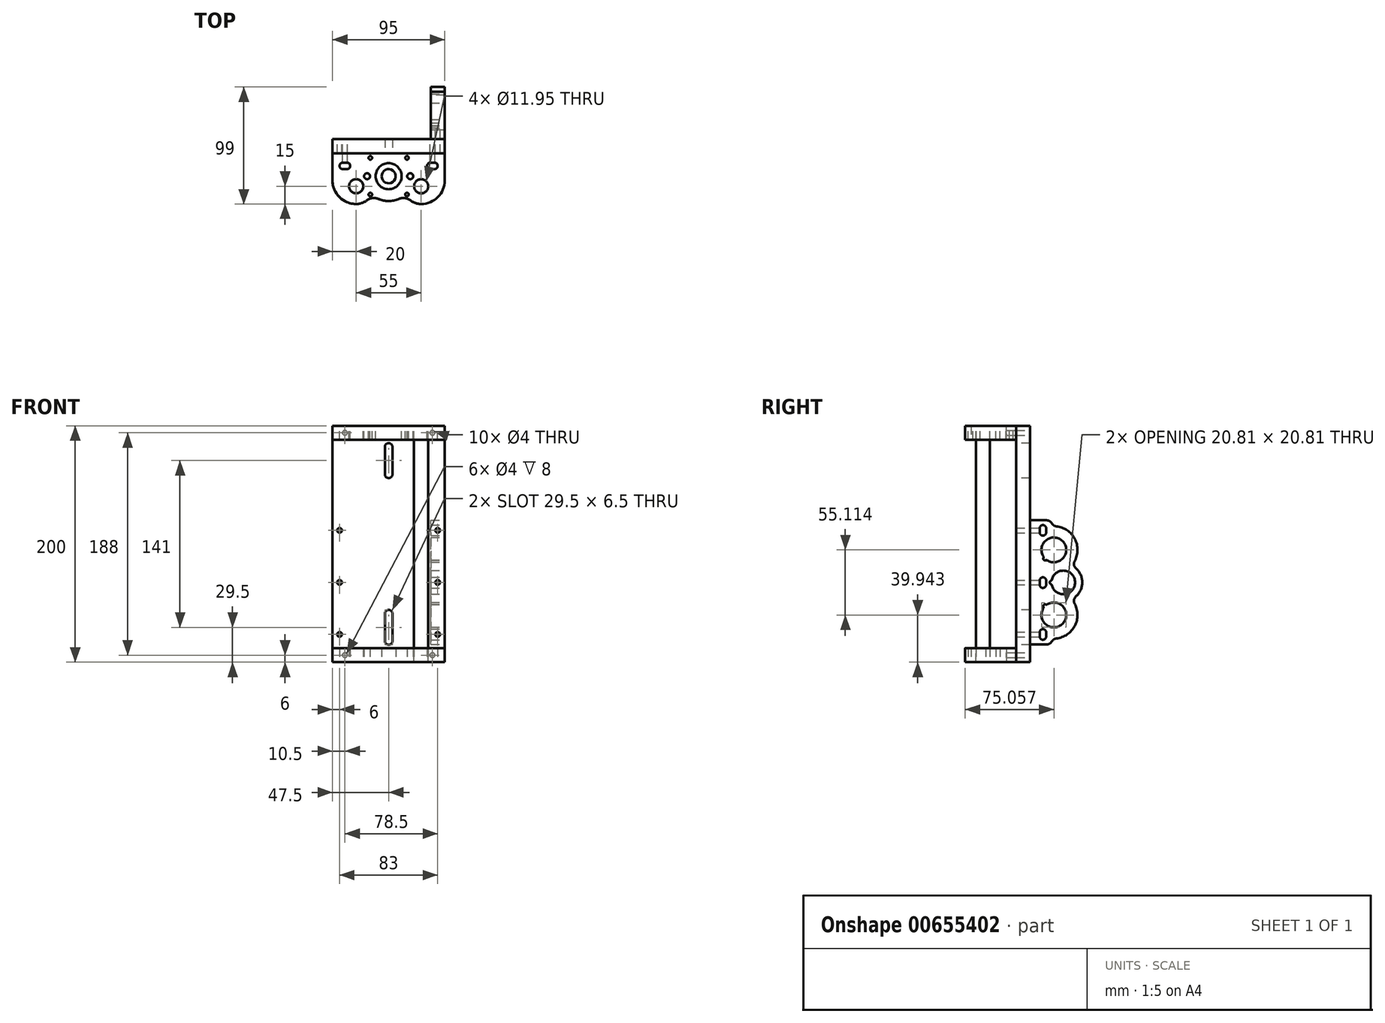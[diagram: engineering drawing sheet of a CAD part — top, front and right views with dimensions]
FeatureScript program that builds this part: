
annotation { "Feature Type Name" : "Feature", "Feature Type Description" : "" }
export const myFeature = defineFeature(function(context is Context, id is Id, definition is map)
    precondition{}
    {
        {
            var Q0;
            Q0=qCreatedBy(makeId("Front.planeOp"),FACE);
            var sketch = newSketch(context, id + "F0", { "sketchPlane" : qUnion([Q0])});
            skLineSegment(sketch, "E0.bottom", {"start": v(47.5, 0) * mm, "end": v(-47.5, 0) * mm});
            skLineSegment(sketch, "E0.top", {"start": v(-47.5, 200) * mm, "end": v(47.5, 200) * mm});
            skLineSegment(sketch, "E0.left", {"start": v(-47.5, 0) * mm, "end": v(-47.5, 200) * mm});
            skLineSegment(sketch, "E0.right", {"start": v(47.5, 0) * mm, "end": v(47.5, 200) * mm});
            skLineSegment(sketch, "E1.left", {"start": v(3.25, 182) * mm, "end": v(3.25, 159) * mm});
            skLineSegment(sketch, "E1.right", {"start": v(-3.25, 182) * mm, "end": v(-3.25, 159) * mm});
            skArc(sketch, "E2", {"start": v(3.25, 182) * mm, "mid": v(0, 185.25) * mm, "end": v(-3.25, 182) * mm});
            skArc(sketch, "E3", {"start": v(-3.25, 159) * mm, "mid": v(0, 155.75) * mm, "end": v(3.25, 159) * mm});
            skLineSegment(sketch, "E4", {"start": v(0, 200) * mm, "end": v(0, 182) * mm, "construction": true});
            skLineSegment(sketch, "E5.left", {"start": v(-3.25, 18) * mm, "end": v(-3.25, 41) * mm});
            skLineSegment(sketch, "E5.right", {"start": v(3.25, 18) * mm, "end": v(3.25, 41) * mm});
            skArc(sketch, "E6", {"start": v(-3.25, 18) * mm, "mid": v(0, 14.75) * mm, "end": v(3.25, 18) * mm});
            skArc(sketch, "E7", {"start": v(3.25, 41) * mm, "mid": v(0, 44.25) * mm, "end": v(-3.25, 41) * mm});
            skLineSegment(sketch, "E8", {"start": v(0, 0) * mm, "end": v(0, 18) * mm, "construction": true});
            skSolve(sketch);
        }
        {
            var Q0;
            Q0=qSketchRegion(id+"F0",true);
            extrude(context, id + "F1", {"entities" : qUnion([Q0]), "oppositeDirection" : true, "depth" : 12 * mm, "offsetDistance" : 25 * mm});
        }
        {
            var Q0;
            Q0=makeQuery(id+"F1.opExtrude","SWEPT_FACE",FACE,{"disambiguationData":[OSD([sQuery(id+"F0.wireOp",EDGE,"E0.top")])]});
            var sketch = newSketch(context, id + "F2", { "sketchPlane" : qUnion([Q0])});
            skLineSegment(sketch, "E9.bottom", {"start": v(-47.5, 0) * mm, "end": v(47.5, 0) * mm});
            skLineSegment(sketch, "E9.top", {"start": v(-27.5, -43) * mm, "end": v(27.5, -43) * mm, "construction": true});
            skLineSegment(sketch, "E9.left", {"start": v(-47.5, 0) * mm, "end": v(-47.5, -23) * mm});
            skLineSegment(sketch, "E9.right", {"start": v(47.5, 0) * mm, "end": v(47.5, -23) * mm});
            skLineSegment(sketch, "E10", {"start": v(0, 0) * mm, "end": v(0, -43) * mm, "construction": true});
            skCircle(sketch, "E11", {"center": v(-27.5, -28) * mm, "radius": 5.97 * mm});
            skCircle(sketch, "E12.MirrorC", {"center": v(27.5, -28) * mm, "radius": 5.97 * mm});
            skArc(sketch, "E13.filletArc", {"start": v(-47.5, -23) * mm, "mid": v(-41.64, -37.14) * mm, "end": v(-27.5, -43) * mm});
            skPoint(sketch, "E14.visualSharp", {"position": v(47.5, -43) * mm});
            skArc(sketch, "E14.filletArc", {"start": v(27.5, -43) * mm, "mid": v(41.64, -37.14) * mm, "end": v(47.5, -23) * mm});
            skCircle(sketch, "E15", {"center": v(0, -19.5) * mm, "radius": 11 * mm});
            skCircle(sketch, "E16", {"center": v(-18.25, -19.5) * mm, "radius": 2.5 * mm});
            skCircle(sketch, "E17.MirrorC", {"center": v(18.25, -19.5) * mm, "radius": 2.5 * mm});
            skLineSegment(sketch, "E18.bottom", {"start": v(-38.75, -8) * mm, "end": v(-35.25, -8) * mm});
            skLineSegment(sketch, "E18.top", {"start": v(-38.75, -13.5) * mm, "end": v(-35.25, -13.5) * mm});
            skArc(sketch, "E19", {"start": v(-38.75, -8) * mm, "mid": v(-41.5, -10.75) * mm, "end": v(-38.75, -13.5) * mm});
            skArc(sketch, "E20", {"start": v(-35.25, -13.5) * mm, "mid": v(-32.5, -10.75) * mm, "end": v(-35.25, -8) * mm});
            skLineSegment(sketch, "E21", {"start": v(-37, -8) * mm, "end": v(-37, -13.5) * mm, "construction": true});
            skArc(sketch, "E22.MirrorCS", {"start": v(35.25, -13.5) * mm, "mid": v(32.5, -10.75) * mm, "end": v(35.25, -8) * mm});
            skLineSegment(sketch, "E23.MirrorCS", {"start": v(38.75, -13.5) * mm, "end": v(35.25, -13.5) * mm});
            skLineSegment(sketch, "E24.MirrorCS", {"start": v(38.75, -8) * mm, "end": v(35.25, -8) * mm});
            skArc(sketch, "E25.MirrorCS", {"start": v(38.75, -8) * mm, "mid": v(41.5, -10.75) * mm, "end": v(38.75, -13.5) * mm});
            skArc(sketch, "E26", {"start": v(-7.8, 0) * mm, "mid": v(0, -40.5) * mm, "end": v(7.8, 0) * mm});
            skCircle(sketch, "E27", {"center": v(-27.5, -28) * mm, "radius": 15 * mm});
            skCircle(sketch, "E28", {"center": v(27.5, -28) * mm, "radius": 15 * mm});
            skSolve(sketch);
        }
        {
            var Q0;
            Q0=qSketchRegion(id+"F2",true);
            extrude(context, id + "F3", {"entities" : qUnion([Q0]), "oppositeDirection" : true, "depth" : 12 * mm, "offsetDistance" : 25 * mm});
        }
        {
            var Q0;
            Q0=makeQuery(id+"F3.opExtrude","SWEPT_EDGE",EDGE,{"disambiguationData":[OSD([sQuery(id+"F2.wireOp",EDGE,"E26"),sQuery(id+"F2.wireOp",EDGE,"E27")])]});
            var Q1;
            Q1=makeQuery(id+"F3.opExtrude","SWEPT_EDGE",EDGE,{"disambiguationData":[OSD([sQuery(id+"F2.wireOp",EDGE,"E26"),sQuery(id+"F2.wireOp",EDGE,"E28")])]});
            fillet(context, id + "F4", {"entities" : qUnion([Q0, Q1]), "radius" : 10 * mm, "tangentPropagation" : true, "allowEdgeOverflow" : false});
        }
        {
            var Q0;
            Q0=makeQuery(id+"F3.opExtrude","CAP_FACE",FACE,{"disambiguationData":[OSD([sQuery(id+"F2.wireOp",EDGE,"E9.bottom"),sQuery(id+"F2.wireOp",EDGE,"E9.top"),sQuery(id+"F2.wireOp",EDGE,"E9.left"),sQuery(id+"F2.wireOp",EDGE,"E9.right"),sQuery(id+"F2.wireOp",EDGE,"E11"),sQuery(id+"F2.wireOp",EDGE,"E12.MirrorC"),sQuery(id+"F2.wireOp",EDGE,"E13.filletArc"),sQuery(id+"F2.wireOp",EDGE,"E14.filletArc")])],"isStart":true});
            var sketch = newSketch(context, id + "F5", { "sketchPlane" : qUnion([Q0])});
            skCircle(sketch, "E29", {"center": v(27.5, -28) * mm, "radius": 6 * mm});
            skSolve(sketch);
        }
        {
            var Q0;
            Q0=qSketchRegion(id+"F5",true);
            extrude(context, id + "F6", {"entities" : qUnion([Q0]), "oppositeDirection" : true, "depth" : 200 * mm, "offsetDistance" : 25 * mm});
        }
        {
            var Q0;
            Q0=makeQuery(id+"F1.opExtrude","SWEPT_FACE",FACE,{"disambiguationData":[OSD([sQuery(id+"F0.wireOp",EDGE,"E0.right")])]});
            var sketch = newSketch(context, id + "F7", { "sketchPlane" : qUnion([Q0])});
            skLineSegment(sketch, "E30.top", {"start": v(52, 40) * mm, "end": v(52, 67.5) * mm, "construction": true});
            skLineSegment(sketch, "E31", {"start": v(12, 67.5) * mm, "end": v(52, 67.5) * mm, "construction": true});
            skPoint(sketch, "E32.centerSnap0", {"position": v(32, 67.5) * mm});
            skArc(sketch, "E33.filletArc", {"start": v(32, 20) * mm, "mid": v(46.14, 25.86) * mm, "end": v(52, 40) * mm});
            skArc(sketch, "E34.filletArc", {"start": v(52, 95) * mm, "mid": v(46.14, 109.14) * mm, "end": v(32, 115) * mm});
            skArc(sketch, "E35", {"start": v(23.22, 45.7) * mm, "mid": v(39.4, 32.6) * mm, "end": v(26.3, 48.78) * mm});
            skArc(sketch, "E36.MirrorC", {"start": v(23.22, 89.3) * mm, "mid": v(39.4, 102.4) * mm, "end": v(26.3, 86.22) * mm});
            skArc(sketch, "E37", {"start": v(47.07, 53.15) * mm, "mid": v(56, 67.5) * mm, "end": v(47.07, 81.85) * mm});
            skArc(sketch, "E38", {"start": v(30.26, 65.33) * mm, "mid": v(49.98, 67.5) * mm, "end": v(30.26, 69.67) * mm});
            skLineSegment(sketch, "E39.bottom", {"start": v(32, 20) * mm, "end": v(28.5, 15) * mm});
            skLineSegment(sketch, "E39.right", {"start": v(28.5, 15) * mm, "end": v(12, 15) * mm});
            skLineSegment(sketch, "E40.bottom", {"start": v(25.5, 25.25) * mm, "end": v(25.5, 21.75) * mm});
            skLineSegment(sketch, "E40.top", {"start": v(20, 25.25) * mm, "end": v(20, 21.75) * mm});
            skArc(sketch, "E41", {"start": v(25.5, 25.25) * mm, "mid": v(22.75, 28) * mm, "end": v(20, 25.25) * mm});
            skArc(sketch, "E42", {"start": v(20, 21.75) * mm, "mid": v(22.75, 19) * mm, "end": v(25.5, 21.75) * mm});
            skLineSegment(sketch, "E43.MirrorCS", {"start": v(32, 115) * mm, "end": v(28.5, 120) * mm});
            skLineSegment(sketch, "E44.MirrorCS", {"start": v(28.5, 120) * mm, "end": v(12, 120) * mm});
            skLineSegment(sketch, "E45.top", {"start": v(20, 69.07) * mm, "end": v(20, 65.57) * mm});
            skArc(sketch, "E46", {"start": v(25.5, 69.07) * mm, "mid": v(22.75, 71.82) * mm, "end": v(20, 69.07) * mm});
            skArc(sketch, "E47", {"start": v(20, 65.57) * mm, "mid": v(22.75, 62.82) * mm, "end": v(25.5, 65.57) * mm});
            skLineSegment(sketch, "E48", {"start": v(20, 23.5) * mm, "end": v(25.5, 23.5) * mm, "construction": true});
            skLineSegment(sketch, "E49.trimOffspring", {"start": v(52, 67.5) * mm, "end": v(52, 95) * mm, "construction": true});
            skLineSegment(sketch, "E50", {"start": v(12, 120) * mm, "end": v(12, 15) * mm});
            skLineSegment(sketch, "E51", {"start": v(32, 40) * mm, "end": v(32, 20) * mm, "construction": true});
            skLineSegment(sketch, "E52", {"start": v(32, 95) * mm, "end": v(32, 40) * mm, "construction": true});
            skArc(sketch, "E53", {"start": v(52, 40) * mm, "mid": v(50.73, 47.02) * mm, "end": v(47.07, 53.15) * mm});
            skArc(sketch, "E54.MirrorCS", {"start": v(52, 95) * mm, "mid": v(50.73, 87.98) * mm, "end": v(47.07, 81.85) * mm});
            skLineSegment(sketch, "E55", {"start": v(32, 95) * mm, "end": v(24.6, 87.6) * mm, "construction": true});
            skArc(sketch, "E56", {"start": v(23.26, 88.29) * mm, "mid": v(23.53, 86.53) * mm, "end": v(25.29, 86.26) * mm});
            skPoint(sketch, "E57.visualSharp", {"position": v(23.61, 88.73) * mm});
            skArc(sketch, "E57.filletArc", {"start": v(23.26, 88.29) * mm, "mid": v(23.38, 88.8) * mm, "end": v(23.22, 89.3) * mm});
            skPoint(sketch, "E58.visualSharp", {"position": v(25.73, 86.61) * mm});
            skArc(sketch, "E58.filletArc", {"start": v(26.3, 86.22) * mm, "mid": v(25.8, 86.38) * mm, "end": v(25.29, 86.26) * mm});
            skArc(sketch, "E59.MirrorCS", {"start": v(26.3, 48.78) * mm, "mid": v(25.8, 48.62) * mm, "end": v(25.29, 48.74) * mm});
            skArc(sketch, "E60.MirrorCS", {"start": v(23.26, 46.71) * mm, "mid": v(23.53, 48.47) * mm, "end": v(25.29, 48.74) * mm});
            skArc(sketch, "E61.MirrorCS", {"start": v(23.26, 46.71) * mm, "mid": v(23.38, 46.2) * mm, "end": v(23.22, 45.7) * mm});
            skLineSegment(sketch, "E62", {"start": v(25.5, 69.07) * mm, "end": v(25.5, 65.57) * mm});
            skArc(sketch, "E63.MirrorCS", {"start": v(25.5, 109.75) * mm, "mid": v(22.75, 107) * mm, "end": v(20, 109.75) * mm});
            skLineSegment(sketch, "E64.MirrorCS", {"start": v(25.5, 109.75) * mm, "end": v(25.5, 113.25) * mm});
            skLineSegment(sketch, "E65.MirrorCS", {"start": v(20, 109.75) * mm, "end": v(20, 113.25) * mm});
            skArc(sketch, "E66.MirrorCS", {"start": v(20, 113.25) * mm, "mid": v(22.75, 116) * mm, "end": v(25.5, 113.25) * mm});
            skArc(sketch, "E67", {"start": v(29.58, 68.93) * mm, "mid": v(28.53, 67.5) * mm, "end": v(29.58, 66.07) * mm});
            skPoint(sketch, "E68.visualSharp", {"position": v(30.14, 69) * mm});
            skArc(sketch, "E68.filletArc", {"start": v(29.58, 68.93) * mm, "mid": v(30.02, 69.21) * mm, "end": v(30.26, 69.67) * mm});
            skPoint(sketch, "E69.visualSharp", {"position": v(30.14, 66) * mm});
            skArc(sketch, "E69.filletArc", {"start": v(30.26, 65.33) * mm, "mid": v(30.02, 65.79) * mm, "end": v(29.58, 66.07) * mm});
            skSolve(sketch);
        }
        {
            var Q0;
            Q0=qSketchRegion(id+"F7",true);
            extrude(context, id + "F8", {"entities" : qUnion([Q0]), "oppositeDirection" : true, "depth" : 12 * mm, "offsetDistance" : 25 * mm});
        }
        {
            var Q0;
            Q0=makeQuery(id+"F1.opExtrude","SWEPT_FACE",FACE,{"disambiguationData":[OSD([sQuery(id+"F0.wireOp",EDGE,"E0.bottom")])]});
            var sketch = newSketch(context, id + "F9", { "sketchPlane" : qUnion([Q0])});
            skLineSegment(sketch, "E70.0", {"start": v(-47.5, 0) * mm, "end": v(47.5, 0) * mm});
            skArc(sketch, "E70.1", {"start": v(47.5, 23) * mm, "mid": v(41.64, 37.14) * mm, "end": v(27.5, 43) * mm});
            skLineSegment(sketch, "E70.3", {"start": v(47.5, 0) * mm, "end": v(47.5, 23) * mm});
            skArc(sketch, "E70.4", {"start": v(-27.5, 43) * mm, "mid": v(-41.64, 37.14) * mm, "end": v(-47.5, 23) * mm});
            skLineSegment(sketch, "E70.5", {"start": v(-47.5, 23) * mm, "end": v(-47.5, 0) * mm});
            skCircle(sketch, "E71.0", {"center": v(-27.5, 28) * mm, "radius": 5.97 * mm});
            skCircle(sketch, "E72.0", {"center": v(27.5, 28) * mm, "radius": 5.97 * mm});
            skCircle(sketch, "E73.0", {"center": v(-18.25, 19.5) * mm, "radius": 2.5 * mm});
            skCircle(sketch, "E74.0", {"center": v(18.25, 19.5) * mm, "radius": 2.5 * mm});
            skCircle(sketch, "E75.0", {"center": v(0, 19.5) * mm, "radius": 6 * mm});
            skArc(sketch, "E76.0", {"start": v(18.43, 39.95) * mm, "mid": v(22.72, 42.22) * mm, "end": v(27.5, 43) * mm});
            skArc(sketch, "E76.1", {"start": v(-27.5, 43) * mm, "mid": v(-22.72, 42.22) * mm, "end": v(-18.43, 39.95) * mm});
            skArc(sketch, "E76.2", {"start": v(-18.43, 39.95) * mm, "mid": v(-13.58, 37.99) * mm, "end": v(-8.4, 38.75) * mm});
            skArc(sketch, "E76.3", {"start": v(-8.4, 38.75) * mm, "mid": v(0, 40.5) * mm, "end": v(8.4, 38.75) * mm});
            skArc(sketch, "E76.4", {"start": v(8.4, 38.75) * mm, "mid": v(13.58, 37.99) * mm, "end": v(18.43, 39.95) * mm});
            skArc(sketch, "E77.0", {"start": v(-38.75, 8) * mm, "mid": v(-41.5, 10.75) * mm, "end": v(-38.75, 13.5) * mm});
            skLineSegment(sketch, "E77.1", {"start": v(-38.75, 8) * mm, "end": v(-35.25, 8) * mm});
            skArc(sketch, "E77.2", {"start": v(-35.25, 13.5) * mm, "mid": v(-32.5, 10.75) * mm, "end": v(-35.25, 8) * mm});
            skLineSegment(sketch, "E77.3", {"start": v(-38.75, 13.5) * mm, "end": v(-35.25, 13.5) * mm});
            skArc(sketch, "E78.0", {"start": v(35.25, 13.5) * mm, "mid": v(32.5, 10.75) * mm, "end": v(35.25, 8) * mm});
            skLineSegment(sketch, "E78.1", {"start": v(38.75, 13.5) * mm, "end": v(35.25, 13.5) * mm});
            skArc(sketch, "E78.2", {"start": v(38.75, 8) * mm, "mid": v(41.5, 10.75) * mm, "end": v(38.75, 13.5) * mm});
            skLineSegment(sketch, "E78.3", {"start": v(38.75, 8) * mm, "end": v(35.25, 8) * mm});
            skSolve(sketch);
        }
        {
            var Q0;
            Q0=qSketchRegion(id+"F9",true);
            extrude(context, id + "F10", {"entities" : qUnion([Q0]), "oppositeDirection" : true, "depth" : 12 * mm, "offsetDistance" : 25 * mm});
        }
        {
            var Q0;
            Q0=makeQuery(id+"F1.opExtrude","CAP_FACE",FACE,{"disambiguationData":[OSD([sQuery(id+"F0.wireOp",EDGE,"E0.bottom"),sQuery(id+"F0.wireOp",EDGE,"E0.top"),sQuery(id+"F0.wireOp",EDGE,"E0.left"),sQuery(id+"F0.wireOp",EDGE,"E0.right")])],"isStart":false});
            var sketch = newSketch(context, id + "F11", { "sketchPlane" : qUnion([Q0])});
            skCircle(sketch, "E79", {"center": v(-37, 194) * mm, "radius": 2 * mm});
            skCircle(sketch, "E80", {"center": v(37, 194) * mm, "radius": 2 * mm});
            skLineSegment(sketch, "E81", {"start": v(-47.5, 100) * mm, "end": v(47.5, 100) * mm, "construction": true});
            skCircle(sketch, "E82.MirrorC", {"center": v(37, 6) * mm, "radius": 2 * mm});
            skCircle(sketch, "E83.MirrorC", {"center": v(-37, 6) * mm, "radius": 2 * mm});
            skCircle(sketch, "E84", {"center": v(-41.5, 23.5) * mm, "radius": 2 * mm});
            skCircle(sketch, "E85", {"center": v(-41.5, 111.5) * mm, "radius": 2 * mm});
            skCircle(sketch, "E86", {"center": v(-41.5, 67.5) * mm, "radius": 2 * mm});
            skLineSegment(sketch, "E87", {"start": v(0, 100) * mm, "end": v(0, 0) * mm, "construction": true});
            skCircle(sketch, "E88.MirrorC", {"center": v(41.5, 23.5) * mm, "radius": 2 * mm});
            skCircle(sketch, "E89.MirrorC", {"center": v(41.5, 111.5) * mm, "radius": 2 * mm});
            skCircle(sketch, "E90.MirrorC", {"center": v(41.5, 67.5) * mm, "radius": 2 * mm});
            skSolve(sketch);
        }
        {
            var Q0;
            Q0=qSketchRegion(id+"F11",true);
            extrude(context, id + "F12", {"entities" : qUnion([Q0]), "operationType" : NewBodyOperationType.REMOVE, "oppositeDirection" : true, "depth" : 25 * mm, "offsetDistance" : 25 * mm, "hasSecondDirection" : true, "secondDirectionOppositeDirection" : false, "secondDirectionDepth" : 10 * mm});
        }
        {
            var Q0;
            Q0=makeQuery(id+"F3.opExtrude","CAP_FACE",FACE,{"disambiguationData":[OSD([sQuery(id+"F2.wireOp",EDGE,"E9.bottom"),sQuery(id+"F2.wireOp",EDGE,"E9.left"),sQuery(id+"F2.wireOp",EDGE,"E9.right"),sQuery(id+"F2.wireOp",EDGE,"E11"),sQuery(id+"F2.wireOp",EDGE,"E12.MirrorC"),sQuery(id+"F2.wireOp",EDGE,"E13.filletArc"),sQuery(id+"F2.wireOp",EDGE,"E14.filletArc"),sQuery(id+"F2.wireOp",EDGE,"E15"),sQuery(id+"F2.wireOp",EDGE,"E16"),sQuery(id+"F2.wireOp",EDGE,"E17.MirrorC"),sQuery(id+"F2.wireOp",EDGE,"E18.bottom"),sQuery(id+"F2.wireOp",EDGE,"E18.top"),sQuery(id+"F2.wireOp",EDGE,"E19"),sQuery(id+"F2.wireOp",EDGE,"E20"),sQuery(id+"F2.wireOp",EDGE,"E22.MirrorCS"),sQuery(id+"F2.wireOp",EDGE,"E23.MirrorCS"),sQuery(id+"F2.wireOp",EDGE,"E24.MirrorCS"),sQuery(id+"F2.wireOp",EDGE,"E25.MirrorCS"),sQuery(id+"F2.wireOp",EDGE,"E26"),sQuery(id+"F2.wireOp",EDGE,"E27"),sQuery(id+"F2.wireOp",EDGE,"E28")])],"isStart":true});
            var sketch = newSketch(context, id + "F13", { "sketchPlane" : qUnion([Q0])});
            skLineSegment(sketch, "E91.bottom", {"start": v(-15.5, -4) * mm, "end": v(15.5, -4) * mm, "construction": true});
            skLineSegment(sketch, "E91.top", {"start": v(-15.5, -35) * mm, "end": v(15.5, -35) * mm, "construction": true});
            skLineSegment(sketch, "E91.left", {"start": v(-15.5, -4) * mm, "end": v(-15.5, -35) * mm, "construction": true});
            skLineSegment(sketch, "E91.right", {"start": v(15.5, -4) * mm, "end": v(15.5, -35) * mm, "construction": true});
            skLineSegment(sketch, "E92", {"start": v(-15.5, -19.5) * mm, "end": v(15.5, -19.5) * mm, "construction": true});
            skPoint(sketch, "E93", {"position": v(0, -19.5) * mm});
            skCircle(sketch, "E94", {"center": v(-15.5, -4) * mm, "radius": 1.5 * mm});
            skCircle(sketch, "E95.1.0", {"center": v(-15.5, -35) * mm, "radius": 1.5 * mm});
            skCircle(sketch, "E95.2.0", {"center": v(15.5, -35) * mm, "radius": 1.5 * mm});
            skCircle(sketch, "E95.3.0", {"center": v(15.5, -4) * mm, "radius": 1.5 * mm});
            skLineSegment(sketch, "E96", {"start": v(-15.5, -4) * mm, "end": v(15.5, -35) * mm, "construction": true});
            skSolve(sketch);
        }
        {
            var Q0;
            Q0=qSketchRegion(id+"F13",true);
            extrude(context, id + "F14", {"entities" : qUnion([Q0]), "operationType" : NewBodyOperationType.REMOVE, "oppositeDirection" : true, "depth" : 25 * mm, "offsetDistance" : 25 * mm});
        }
        {
            var Q0;
            Q0=makeQuery(id+"F8.opExtrude","SWEPT_EDGE",EDGE,{"disambiguationData":[OSD([sQuery(id+"F7.wireOp",EDGE,"E33.filletArc"),sQuery(id+"F7.wireOp",EDGE,"E39.bottom")])]});
            var Q1;
            Q1=makeQuery(id+"F8.opExtrude","SWEPT_EDGE",EDGE,{"disambiguationData":[OSD([sQuery(id+"F7.wireOp",EDGE,"E39.bottom"),sQuery(id+"F7.wireOp",EDGE,"E39.right")])]});
            var Q2;
            Q2=makeQuery(id+"F8.opExtrude","SWEPT_EDGE",EDGE,{"disambiguationData":[OSD([sQuery(id+"F7.wireOp",EDGE,"E34.filletArc"),sQuery(id+"F7.wireOp",EDGE,"E43.MirrorCS")])]});
            var Q3;
            Q3=makeQuery(id+"F8.opExtrude","SWEPT_EDGE",EDGE,{"disambiguationData":[OSD([sQuery(id+"F7.wireOp",EDGE,"E43.MirrorCS"),sQuery(id+"F7.wireOp",EDGE,"E44.MirrorCS")])]});
            fillet(context, id + "F15", {"entities" : qUnion([Q0, Q1, Q2, Q3]), "radius" : 5 * mm, "tangentPropagation" : true, "allowEdgeOverflow" : false});
        }
        {
            var Q0;
            Q0=makeQuery(id+"F8.opExtrude","SWEPT_EDGE",EDGE,{"disambiguationData":[OSD([sQuery(id+"F7.wireOp",EDGE,"E37"),sQuery(id+"F7.wireOp",EDGE,"E54.MirrorCS")])]});
            var Q1;
            Q1=makeQuery(id+"F8.opExtrude","SWEPT_EDGE",EDGE,{"disambiguationData":[OSD([sQuery(id+"F7.wireOp",EDGE,"E37"),sQuery(id+"F7.wireOp",EDGE,"E53")])]});
            var Q2;
            Q2=makeQuery(id+"F8.opExtrude","SWEPT_EDGE",EDGE,{"disambiguationData":[OSD([sQuery(id+"F7.wireOp",EDGE,"E38"),sQuery(id+"F7.wireOp",EDGE,"E45.bottom"),sQuery(id+"F7.wireOp",EDGE,"E46")])]});
            var Q3;
            Q3=makeQuery(id+"F8.opExtrude","SWEPT_EDGE",EDGE,{"disambiguationData":[OSD([sQuery(id+"F7.wireOp",EDGE,"E38"),sQuery(id+"F7.wireOp",EDGE,"E45.bottom"),sQuery(id+"F7.wireOp",EDGE,"E47")])]});
            fillet(context, id + "F16", {"entities" : qUnion([Q0, Q1, Q2, Q3]), "radius" : 5 * mm, "tangentPropagation" : true, "allowEdgeOverflow" : false});
        }
    });
